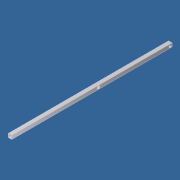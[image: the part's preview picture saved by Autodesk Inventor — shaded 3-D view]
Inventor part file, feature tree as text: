
AUTODESK INVENTOR PART (.ipt)
format: ipt  version: 2012 (Build 160160000, 160)  size: 99,840 bytes
history: native  units: in
note: dims shown in document units (in); Inventor stores cm internally (conversion verified against a paired STEP export)
features: extrude x3, sketch x3, shell x1, plane x1, pattern_linear x1, other x1
ambient origin geometry x8: Origin, YZ Plane, XZ Plane, XY Plane, X Axis, Y Axis, Z Axis, Center Point
bodies: Solid1 (feature_tree)
feature tree (10):
  extrude  "Extrusion1"  Depth=1.75in
  shell  "Shell1"  Thickness=78.0in
  extrude  "Extrusion2"  Depth=1.4375in
  extrude  "Extrusion3"  Depth=0.875in
  plane  "Work Plane1"
  pattern_linear  "Rectangular Pattern1"  Spacing1=78.0in  [1 undecoded]
  sketch  "Sketch1"  dims[d0=1.75in d1=1.75in d2=78.0in d3=0.0in]
  sketch  "Sketch2"  dims[d4=0.125in d5=1.4375in]
  sketch  "Sketch3"  dims[d6=1.75in d7=0.875in d9=78.0in d10=0.0in d11=0.375in d12=1.75in d13=0.875in d14=78.0in d15=0.0in d16=1.4375in d17=0.875in d18=35.0in d19=0.0in d20=0.7874in d22=35.0in]
  other  "Work Axis1"
note: 1 required parameter value undecoded (feature->parameter linkage not recoverable at this tier; creation-order binding heuristic only, values carry confidence <= 0.55)
